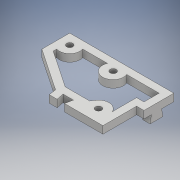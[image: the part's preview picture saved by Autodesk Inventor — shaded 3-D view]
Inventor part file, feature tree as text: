
AUTODESK INVENTOR PART (.ipt)
format: ipt  version: 2017 (Build 210142000, 142)  size: 385,536 bytes
history: native  units: mm
features: extrude x28, sketch x28, shell x2
ambient origin geometry x8: Origin, YZ Plane, XZ Plane, XY Plane, X Axis, Y Axis, Z Axis, Center Point
bodies: Solid1 (feature_tree)
feature tree (58):
  extrude  "Extrusion1"  Depth=37.0mm
  shell  "Shell1"  Thickness=20.0mm
  extrude  "Extrusion2"  Depth=55.0mm
  extrude  "Extrusion3"  TaperAngle=0.0deg  [1 undecoded]
  extrude  "Extrusion4"  Depth=5.0mm
  extrude  "Extrusion5"  TaperAngle=0.0deg  [1 undecoded]
  extrude  "Extrusion6"  Depth=10.0mm TaperAngle=0.0deg
  extrude  "Extrusion7"  Depth=15.0mm TaperAngle=0.0deg
  extrude  "Extrusion9"  Depth=8.5mm
  extrude  "Extrusion10"  Depth=15.0mm TaperAngle=0.0deg
  extrude  "Extrusion11"  Depth=35.46mm
  extrude  "Extrusion12"  Depth=15.0mm TaperAngle=0.0deg
  extrude  "Extrusion13"  Depth=4.5mm
  extrude  "Extrusion14"  Depth=15.0mm TaperAngle=0.0deg
  extrude  "Extrusion15"  Depth=8.5mm
  extrude  "Extrusion16"  Depth=15.0mm TaperAngle=0.0deg
  extrude  "Extrusion17"  Depth=28.505mm
  extrude  "Extrusion18"  Depth=15.0mm TaperAngle=0.0deg
  extrude  "Extrusion19"  Depth=36.0mm
  extrude  "Extrusion20"  Depth=15.0mm TaperAngle=0.0deg
  extrude  "Extrusion22"  Depth=5.0mm
  shell  "Shell2"  Thickness=21.0mm
  extrude  "Extrusion23"  Depth=23.505mm
  extrude  "Extrusion24"  Depth=10.0mm TaperAngle=0.0deg
  extrude  "Extrusion25"  Depth=36.0mm
  extrude  "Extrusion26"  Depth=10.0mm
  extrude  "Extrusion27"  Depth=2.583mm TaperAngle=0.0deg
  extrude  "Extrusion28"  Depth=6.917mm
  extrude  "Extrusion29"  Depth=5.0mm
  extrude  "Extrusion30"  Depth=5.0mm
  sketch  "Sketch1"  dims[d0=35.0mm d1=37.0mm d2=20.0mm]
  sketch  "Sketch2"  dims[d3=11.0mm d4=55.0mm]
  sketch  "Sketch3"  dims[d5=26.0mm d6=0.0mm]
  sketch  "Sketch4"  dims[d7=50.0mm d8=0.0mm d9=5.0mm]
  sketch  "Sketch5"  dims[d10=17.0mm d11=0.0mm]
  sketch  "Sketch6"  dims[d12=11.0mm d13=10.0mm d14=0.0mm]
  sketch  "Sketch7"  dims[d15=15.0mm d16=0.0mm d17=15.0mm d18=0.0mm]
  sketch  "Sketch13"  dims[d19=4.1656mm d20=8.5mm]
  sketch  "Sketch14"  dims[d21=11.5mm d22=15.0mm d23=0.0mm]
  sketch  "Sketch15"  dims[d24=4.1656mm d25=35.46mm]
  sketch  "Sketch16"  dims[d26=23.505mm d27=15.0mm d28=0.0mm]
  sketch  "Sketch17"  dims[d29=4.1656mm d30=4.5mm]
  sketch  "Sketch18"  dims[d31=14.0mm d32=15.0mm d33=0.0mm]
  sketch  "Sketch20"  dims[d41=4.1656mm d42=8.5mm]
  sketch  "Sketch21"  dims[d43=11.5mm d44=15.0mm d45=0.0mm]
  sketch  "Sketch22"  dims[d46=4.1656mm d47=28.505mm]
  sketch  "Sketch23"  dims[d48=35.46mm d49=15.0mm d50=0.0mm]
  sketch  "Sketch24"  dims[d51=4.1656mm d52=36.0mm]
  sketch  "Sketch25"  dims[d53=4.5mm d54=15.0mm d55=0.0mm]
  sketch  "Sketch28"  dims[d56=5.0mm d57=50.0mm d58=21.0mm d59=0.0mm]
  sketch  "Sketch29"  dims[d60=4.1656mm d61=23.505mm]
  sketch  "Sketch30"  dims[d62=35.46mm d63=10.0mm d64=0.0mm]
  sketch  "Sketch31"  dims[d65=4.1656mm d67=36.0mm]
  sketch  "Sketch32"  dims[d68=10.0mm d69=0.0mm d70=4.5mm]
  sketch  "Sketch33"  dims[d71=2.583mm d72=0.0mm d73=2.583mm d74=0.0mm]
  sketch  "Sketch34"  dims[d75=2.583mm d76=0.0mm d77=6.917mm]
  sketch  "Sketch35"  dims[d78=100.0mm d79=0.0mm d80=5.0mm]
  sketch  "Sketch36"  dims[d81=5.0mm d83=1.0mm d84=1.0mm d85=100.0mm d86=0.0mm d87=100.0mm d88=0.0mm d89=5.0mm d111=8.6943mm d112=13.962634mm d113=29.670597mm d114=5.0mm d115=0.0mm d116=7.437911mm d117=5.0mm d118=5.0mm d119=0.0mm d121=5.0mm d122=0.0mm d123=5.0mm d124=5.0mm d125=5.0mm d126=5.0mm d127=5.0mm d128=15.0mm d129=0.0mm d130=5.0mm d131=5.0mm d132=15.0mm d133=0.0mm d134=135.0deg d135=10.0mm d136=0.0mm d137=10.0mm d138=0.0mm d139=5.0mm d140=5.0mm d141=0.0mm d142=5.0mm d143=5.0mm d144=0.0mm]
note: 2 required parameter values undecoded (feature->parameter linkage not recoverable at this tier; creation-order binding heuristic only, values carry confidence <= 0.55)
